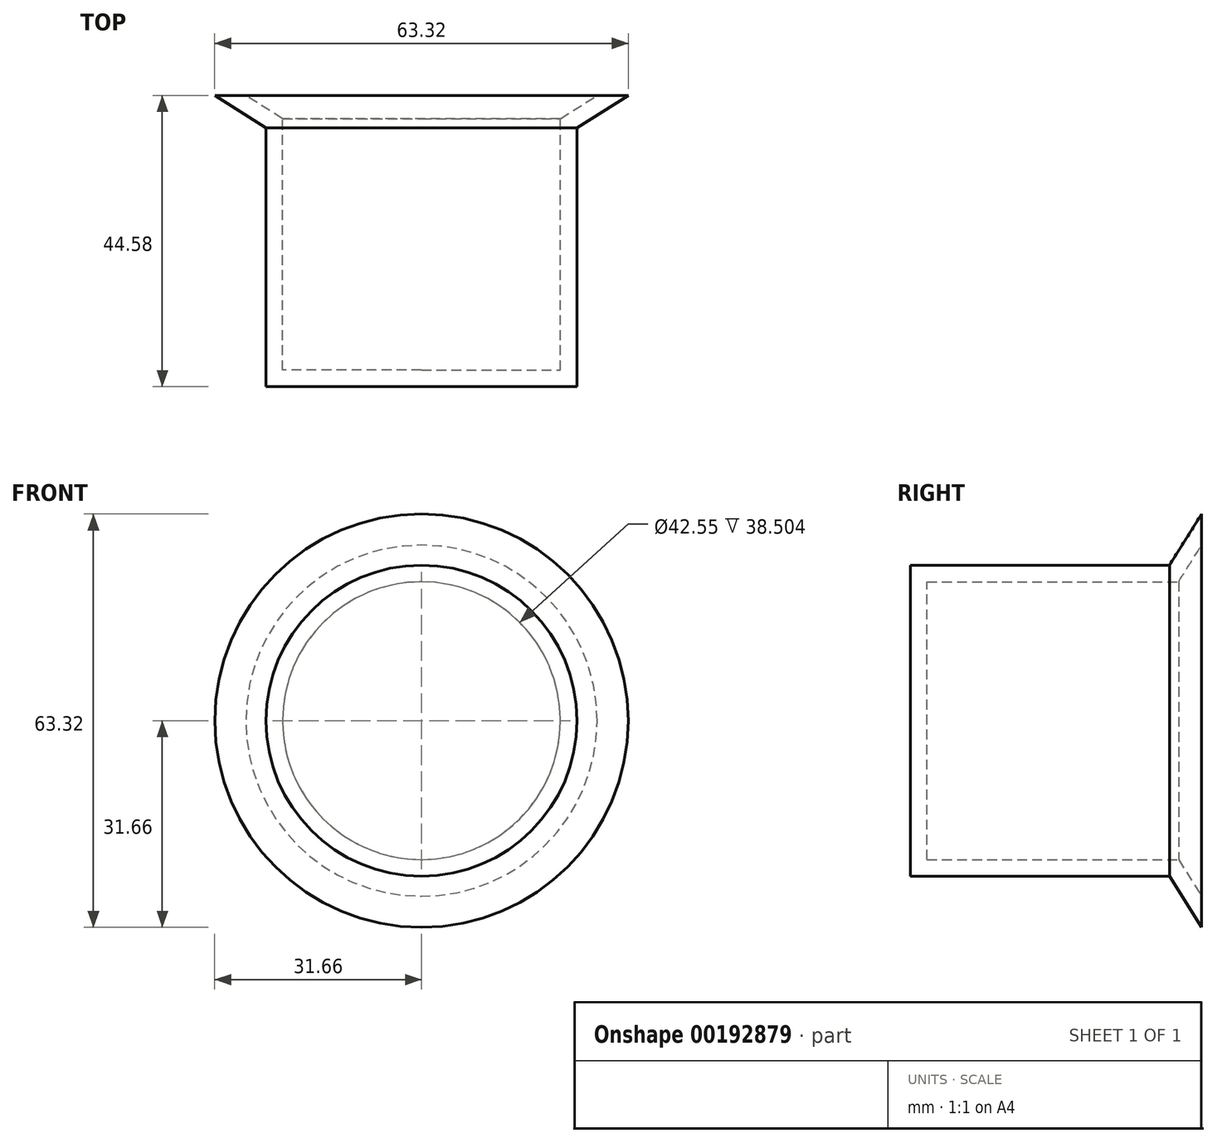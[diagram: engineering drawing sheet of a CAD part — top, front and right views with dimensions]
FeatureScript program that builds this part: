
annotation { "Feature Type Name" : "Feature", "Feature Type Description" : "" }
export const myFeature = defineFeature(function(context is Context, id is Id, definition is map)
    precondition{}
    {
        {
            var Q0;
            Q0=qCreatedBy(makeId("Top.planeOp"),FACE);
            var sketch = newSketch(context, id + "F0", { "sketchPlane" : qUnion([Q0])});
            skLineSegment(sketch, "E0", {"start": v(0, 44.58) * mm, "end": v(31.66, 44.58) * mm});
            skLineSegment(sketch, "E1", {"start": v(31.66, 44.58) * mm, "end": v(23.81, 39.64) * mm});
            skLineSegment(sketch, "E2", {"start": v(23.81, 39.64) * mm, "end": v(23.81, 0) * mm});
            skLineSegment(sketch, "E3", {"start": v(23.81, 0) * mm, "end": v(0, 0) * mm});
            skLineSegment(sketch, "E4", {"start": v(0, 44.58) * mm, "end": v(0, 0) * mm});
            skSolve(sketch);
        }
        {
            var Q0;
            Q0 = qSketchRegion(id + "F0", true);
            var Q1;
            Q1=sQuery(id+"F0.wireOp",EDGE,"E4");
            revolve(context, id + "F1", {"entities" : qUnion([Q0]), "axis" : qUnion([Q1]), "revolveType" : RevolveType.FULL});
        }
        {
            var Q0;
            Q0=makeQuery(id+"F1.opRevolve","SWEPT_FACE",FACE,{"disambiguationData":[OSD([sQuery(id+"F0.wireOp",EDGE,"E0")])]});
            shell(context, id + "F2", {"entities" : qUnion([Q0]), "thickness" : 2.54 * mm});
        }
    });
